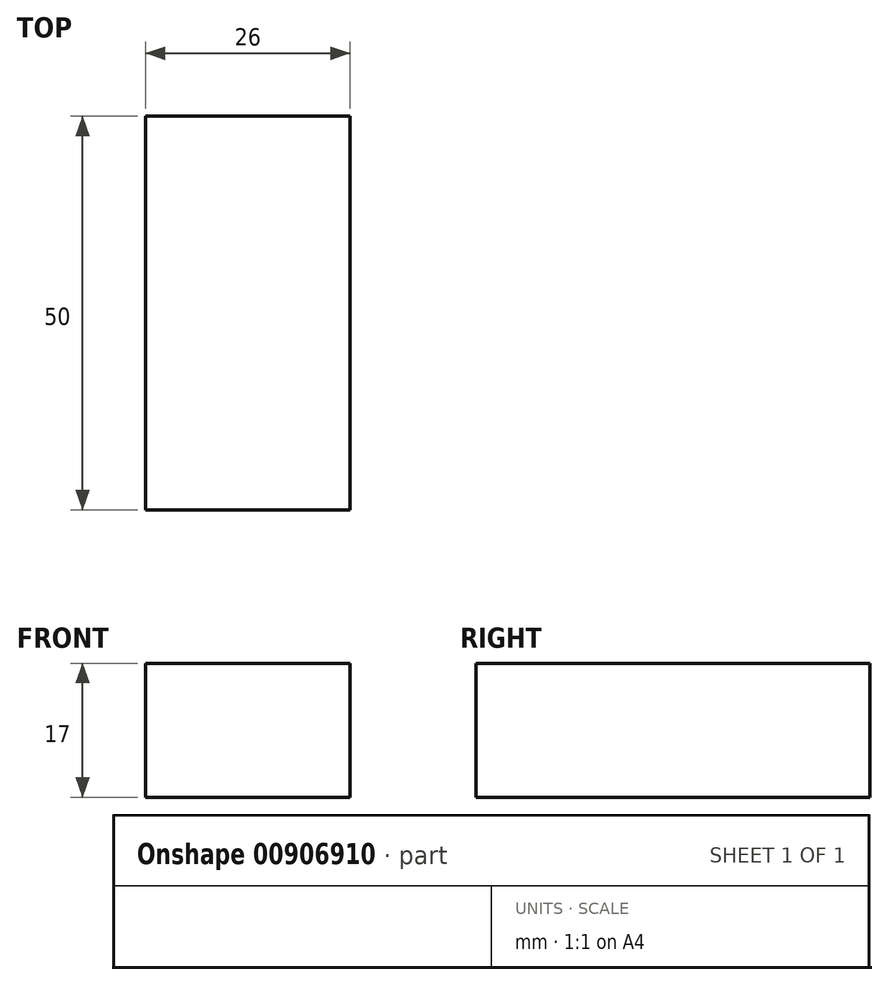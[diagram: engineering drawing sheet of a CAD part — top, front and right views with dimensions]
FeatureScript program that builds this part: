
annotation { "Feature Type Name" : "Feature", "Feature Type Description" : "" }
export const myFeature = defineFeature(function(context is Context, id is Id, definition is map)
    precondition{}
    {
        {
            var Q0;
            Q0=qCreatedBy(makeId("Top.planeOp"),FACE);
            var sketch = newSketch(context, id + "F0", { "sketchPlane" : qUnion([Q0])});
            skLineSegment(sketch, "E0.bottom", {"start": v(13, -25) * mm, "end": v(-13, -25) * mm});
            skLineSegment(sketch, "E0.top", {"start": v(13, 25) * mm, "end": v(-13, 25) * mm});
            skLineSegment(sketch, "E0.left", {"start": v(13, -25) * mm, "end": v(13, 25) * mm});
            skLineSegment(sketch, "E0.right", {"start": v(-13, -25) * mm, "end": v(-13, 25) * mm});
            skPoint(sketch, "E0.middle", {"position": v(0, 0) * mm});
            skSolve(sketch);
        }
        {
            var Q0;
            Q0=makeQuery(id+"F0.imprint","IMPRINT",FACE,{"disambiguationData":[TD([[makeQuery(id+"F0.imprint","IMPRINT",EDGE,{"derivedFrom":sQuery(id+"F0.wireOp",EDGE,"E0.bottom")}),-1.0]])]});
            extrude(context, id + "F1", {"entities" : qUnion([Q0]), "depth" : 17 * mm, "offsetDistance" : 25.4 * mm});
        }
    });
